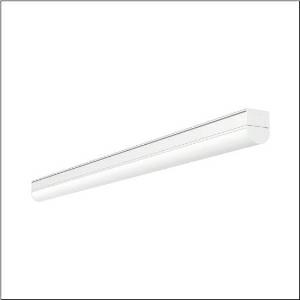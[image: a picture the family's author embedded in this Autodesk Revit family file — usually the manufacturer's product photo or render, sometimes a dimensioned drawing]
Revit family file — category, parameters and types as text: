
# Revit family: ecopack_31_51lj12dnm80a
name_source: partatom
category: Lighting Fixtures
units: mm (PartAtom-declared; Revit-internal decimal feet)

## family parameters
Cut with Voids When Loaded = No
Host = Face
Light Source = No
Part Type = Normal
Room Calculation Point = No
Round Connector Dimension = Use Diameter
Shared = No

## types (1)
- --- (1 x LED, 6780 lm, 52 W, 5000K)
    Apparent Load = 52 VA
    CIE Flux Codes = 39 67 87 89 100
    Color Rendering = 80
    Color Temperature = 5000K
    Default Elevation = 1800 mm
    Description = Ecopack 31, diffuser luminaire, primary optical cover: cover, of PC, frosted, light emission: direct distribution, primary light characteristic: symmetric, installation type: surface-mounted, LED, rated luminous flux: 7.000lm, luminous efficacy: 135lm/W, light colour: 830/840/850, colour temperature: 3000/4000/5000K, control gear: DALI 2, with terminal, 5-pole, mains connection: 220..240V, AC, 50/60Hz, rated input power: 52W, housing, of aluminium, traffic white (RAL 9016), length: 1.450mm, width: 56mm, height: 68mm, end cap, of PC, white, protection rating (complete): IP20, insulation class (complete): insulation class I (protective earthing), certification: CE, impact resistance: IK06, permissible operating ambient temperature: -20..+40°C, packaging unit: 1 piece
    Height = 68 mm
    Lamp = 1 x LED
    Lamp Light Flux = 6780 lm
    Lamp Power = 52 W
    Lamp count = 1
    Length = 1450 mm
    Luminous efficacy = 130 lm/W
    Manufacturer = Siteco
    ModVariant = No
    Model = 51LJ12DNM80A
    Mounting Place = Ceiling
    Mounting Type = Surface mounted
    Number of Poles = 1
    OnlyDefault = Yes
    Power Factor = 1
    Product Name = Ecopack 31
    Product group = diffuser luminaire
    ProductGroupID = 307
    Protection Class = Protection class I
    Protection Degree = IP 20
    RLX_Detail_Level = 1
    RLX_Emergency_Light_Flux = 0 lm
    RLX_Emergency_Type = 0
    RLX_Emergency_Type_DB = No
    RlxData = <blob elided: 21621 chars, md5=532bc659>
    Socket = socket
    Standby Power = 0 W
    System Light Flux = 6780 lm
    System Power = 52 W
    Type Comments = individual setting: colour temperature 5000K
    Type Image = l_1007033.jpg
    URL = http://relux.com
    VarID = @adj_173429
    Voltage = 0 V
    Weight = 0.00 kg
    Width = 56 mm

## geometry (parser evidence)
native form markers: Blend x4, Sweep x12
no freeform markers — native parametric forms only
